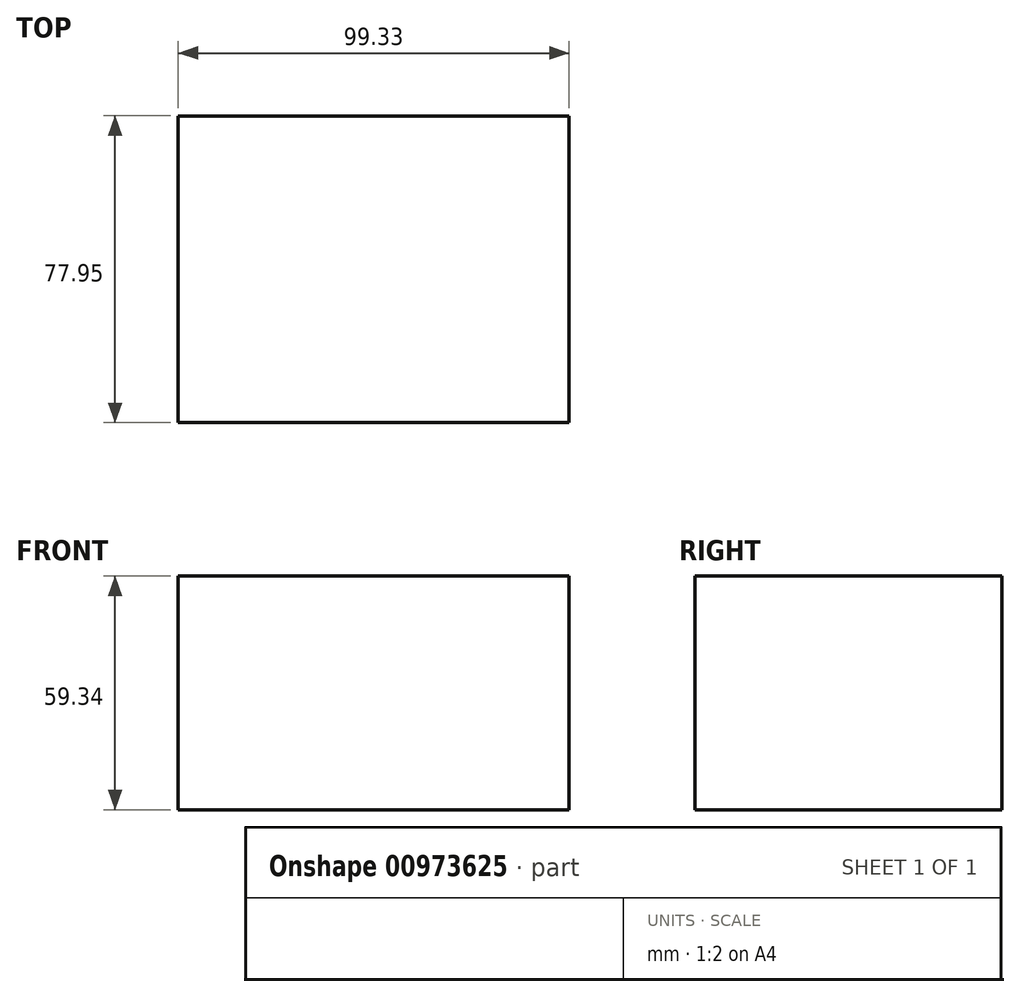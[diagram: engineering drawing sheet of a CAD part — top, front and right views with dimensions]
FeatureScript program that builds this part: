
annotation { "Feature Type Name" : "Feature", "Feature Type Description" : "" }
export const myFeature = defineFeature(function(context is Context, id is Id, definition is map)
    precondition{}
    {
        {
            var Q0;
            Q0=qCreatedBy(makeId("Top.planeOp"),FACE);
            var sketch = newSketch(context, id + "F0", { "sketchPlane" : qUnion([Q0])});
            skLineSegment(sketch, "E0.bottom", {"start": v(-44.73, 38.22) * mm, "end": v(54.6, 38.22) * mm});
            skLineSegment(sketch, "E0.top", {"start": v(-44.73, -39.73) * mm, "end": v(54.6, -39.73) * mm});
            skLineSegment(sketch, "E0.left", {"start": v(-44.73, 38.22) * mm, "end": v(-44.73, -39.73) * mm});
            skLineSegment(sketch, "E0.right", {"start": v(54.6, 38.22) * mm, "end": v(54.6, -39.73) * mm});
            skSolve(sketch);
        }
        {
            var Q0;
            Q0=makeQuery(id+"F0.imprint","IMPRINT",FACE,{"disambiguationData":[TD([[makeQuery(id+"F0.imprint","IMPRINT",EDGE,{"derivedFrom":sQuery(id+"F0.wireOp",EDGE,"E0.bottom")}),-1.0]])]});
            extrude(context, id + "F1", {"entities" : qUnion([Q0]), "depth" : 59.34 * mm, "offsetDistance" : 25.4 * mm});
        }
        {
            var Q0;
            Q0=makeQuery(id+"F1.opExtrude","CAP_FACE",FACE,{"disambiguationData":[OSD([sQuery(id+"F0.wireOp",EDGE,"E0.bottom"),sQuery(id+"F0.wireOp",EDGE,"E0.top"),sQuery(id+"F0.wireOp",EDGE,"E0.left"),sQuery(id+"F0.wireOp",EDGE,"E0.right")])],"isStart":false});
            var sketch = newSketch(context, id + "F2", { "sketchPlane" : qUnion([Q0])});
            skLineSegment(sketch, "E1.bottom", {"start": v(21.13, 38.22) * mm, "end": v(41.43, 38.22) * mm});
            skLineSegment(sketch, "E1.top", {"start": v(21.13, -39.73) * mm, "end": v(41.43, -39.73) * mm});
            skLineSegment(sketch, "E1.left", {"start": v(21.13, 38.22) * mm, "end": v(21.13, -39.73) * mm});
            skLineSegment(sketch, "E1.right", {"start": v(41.43, 38.22) * mm, "end": v(41.43, -39.73) * mm});
            skLineSegment(sketch, "E2.bottom", {"start": v(54.6, 20.8) * mm, "end": v(-44.73, 20.8) * mm});
            skLineSegment(sketch, "E2.top", {"start": v(54.6, -28.4) * mm, "end": v(-44.73, -28.4) * mm});
            skLineSegment(sketch, "E2.left", {"start": v(54.6, 20.8) * mm, "end": v(54.6, -28.4) * mm});
            skLineSegment(sketch, "E2.right", {"start": v(-44.73, 20.8) * mm, "end": v(-44.73, -28.4) * mm});
            skSolve(sketch);
        }
        {
            var Q0;
            Q0=makeQuery(id+"F1.opExtrude","SWEPT_FACE",FACE,{"disambiguationData":[OSD([sQuery(id+"F0.wireOp",EDGE,"E0.top")])]});
            var sketch = newSketch(context, id + "F3", { "sketchPlane" : qUnion([Q0])});
            skArc(sketch, "E3", {"start": v(54.6, 59.34) * mm, "mid": v(4.94, 109) * mm, "end": v(-44.73, 59.34) * mm});
            skSolve(sketch);
        }
        {
            var Q0;
            Q0=sQuery(id+"F2.wireOp",VERTEX,"E1.bottom.start");
            var Q1;
            Q1=makeQuery(id+"F1.opExtrude","SWEPT_FACE",FACE,{"disambiguationData":[OSD([sQuery(id+"F0.wireOp",EDGE,"E0.bottom")])]});
            cPlane(context, id + "F4", {"entities" : qUnion([Q0, Q1]), "cplaneType" : CPlaneType.PLANE_POINT, "offset" : 25.4 * mm, "width" : 152.4 * mm, "height" : 152.4 * mm});
        }
    });
